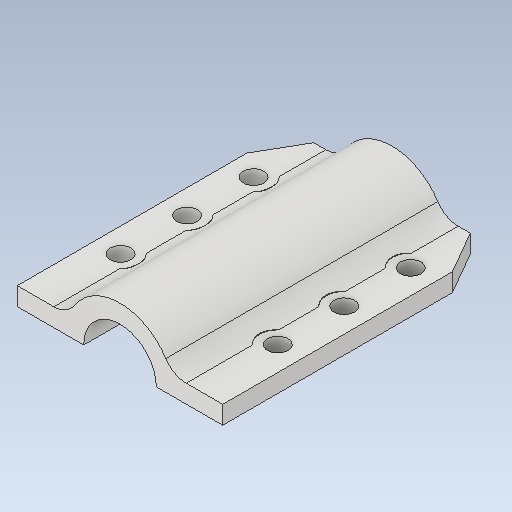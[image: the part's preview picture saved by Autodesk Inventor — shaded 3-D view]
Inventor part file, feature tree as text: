
AUTODESK INVENTOR PART (.ipt)
format: ipt  version: 2020 (Build 240168000, 168)  size: 238,080 bytes
history: native  units: mm
features: extrude x8, sketch x8, other x2, chamfer x2, fillet x1, mirror x1
ambient origin geometry x8: Origin, YZ Plane, XZ Plane, XY Plane, X Axis, Y Axis, Z Axis, Center Point
bodies: Body1 (feature_tree)
feature tree (22):
  other  "Bryła1"
  extrude  "Wyciągnięcie proste1"  Depth=12.0mm
  extrude  "Wyciągnięcie proste2"  Depth=18.0mm
  other  "Płaszczyzna konstrukcyjna1"
  extrude  "Wyciągnięcie proste3"  Depth=50.0mm TaperAngle=0.0deg
  extrude  "Wyciągnięcie proste4"  Depth=3.0mm
  fillet  "Zaokrąglenie1"  Radius=7.2mm
  mirror  "Odbij1"
  extrude  "Wyciągnięcie proste5"  Depth=20.0mm
  extrude  "Wyciągnięcie proste6"  Depth=50.0mm TaperAngle=0.0deg
  chamfer  "Faza2"  [1 undecoded]
  chamfer  "Faza3"  Distance=50.0mm
  extrude  "Wyciągnięcie proste7"  Depth=3.4mm
  extrude  "Wyciągnięcie proste9"  Depth=3.4mm
  sketch  "Szkic1"
  sketch  "Szkic2"
  sketch  "Szkic3"
  sketch  "Szkic5"
  sketch  "Szkic6"
  sketch  "Szkic8"
  sketch  "Szkic9"
  sketch  "Szkic11"
note: 1 required parameter value undecoded (feature->parameter linkage not recoverable at this tier; creation-order binding heuristic only, values carry confidence <= 0.55)
